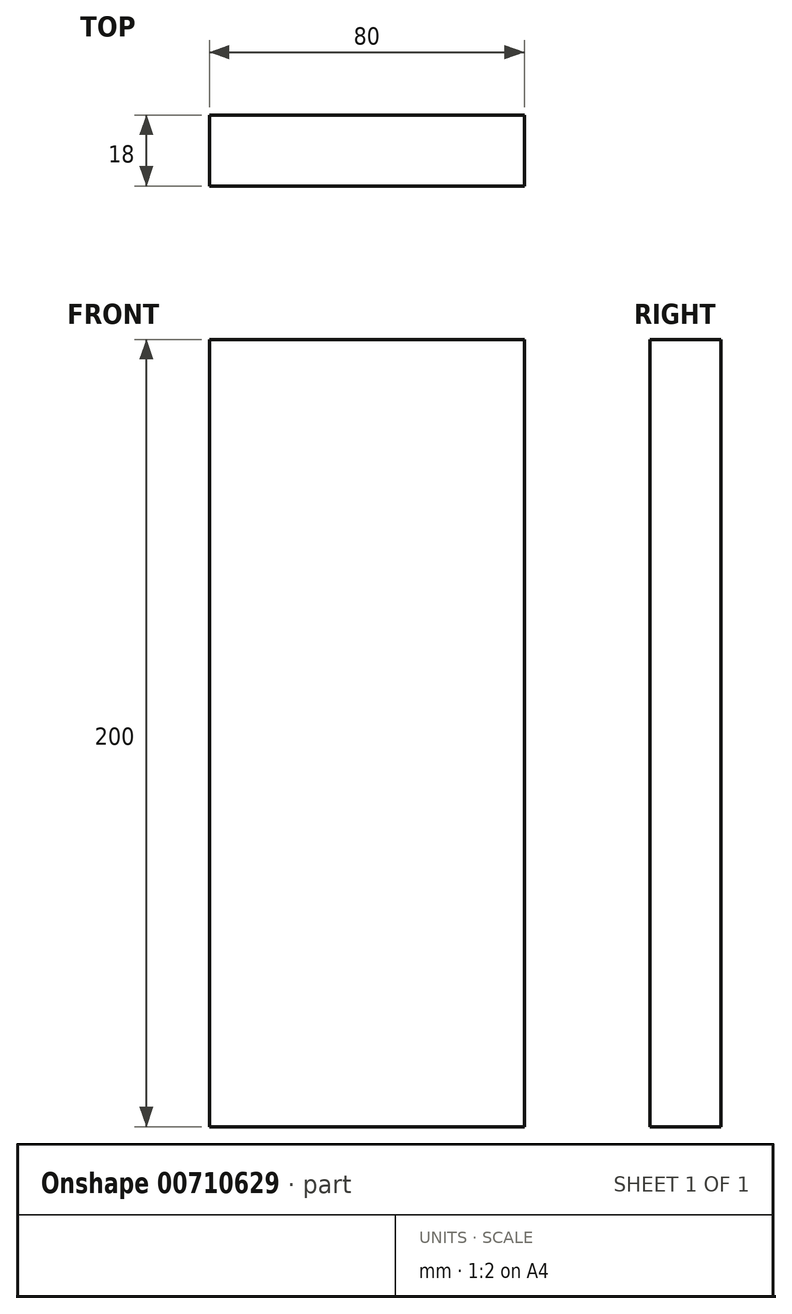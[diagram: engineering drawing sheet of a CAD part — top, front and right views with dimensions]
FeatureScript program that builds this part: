
annotation { "Feature Type Name" : "Feature", "Feature Type Description" : "" }
export const myFeature = defineFeature(function(context is Context, id is Id, definition is map)
    precondition{}
    {
        {
            var Q0;
            Q0=qCreatedBy(makeId("Front.planeOp"),FACE);
            var sketch = newSketch(context, id + "F0", { "sketchPlane" : qUnion([Q0])});
            skLineSegment(sketch, "E0.bottom", {"start": v(0, 0) * mm, "end": v(80, 0) * mm});
            skLineSegment(sketch, "E0.top", {"start": v(0, 200) * mm, "end": v(80, 200) * mm});
            skLineSegment(sketch, "E0.left", {"start": v(0, 0) * mm, "end": v(0, 200) * mm});
            skLineSegment(sketch, "E0.right", {"start": v(80, 0) * mm, "end": v(80, 200) * mm});
            skSolve(sketch);
        }
        {
            var Q0;
            Q0=makeQuery(id+"F0.imprint","IMPRINT",FACE,{"disambiguationData":[TD([[makeQuery(id+"F0.imprint","IMPRINT",EDGE,{"derivedFrom":sQuery(id+"F0.wireOp",EDGE,"E0.bottom")}),1.0]])]});
            extrude(context, id + "F1", {"entities" : qUnion([Q0]), "depth" : 18 * mm, "offsetDistance" : 25 * mm});
        }
    });
